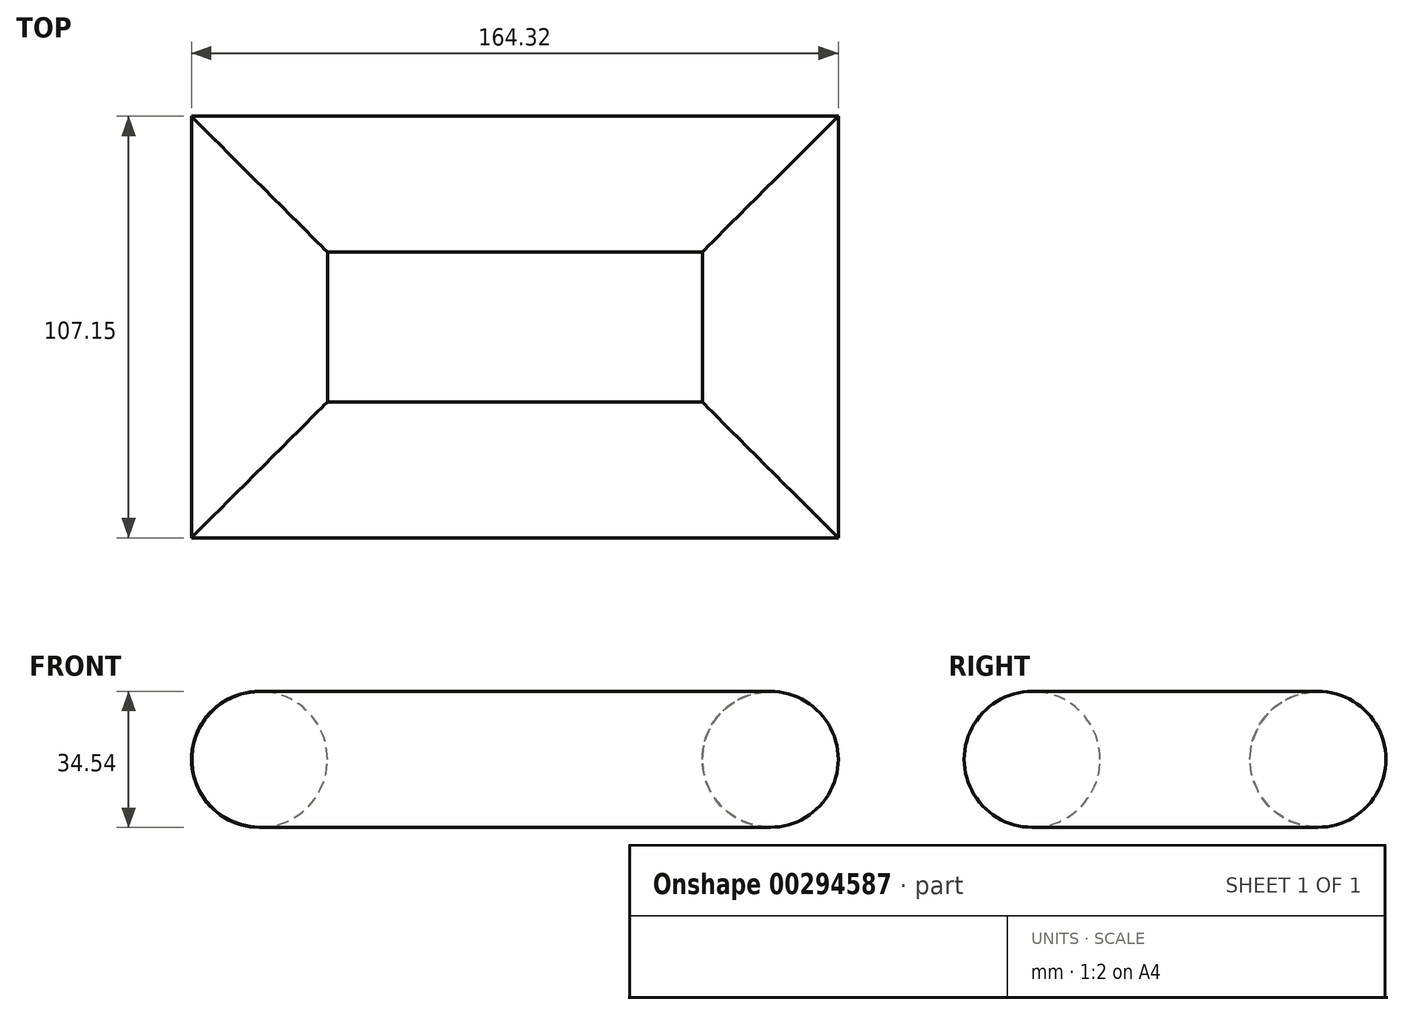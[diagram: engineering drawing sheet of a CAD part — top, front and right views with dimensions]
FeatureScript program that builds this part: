
annotation { "Feature Type Name" : "Feature", "Feature Type Description" : "" }
export const myFeature = defineFeature(function(context is Context, id is Id, definition is map)
    precondition{}
    {
        {
            var Q0;
            Q0=qCreatedBy(makeId("Top.planeOp"),FACE);
            var sketch = newSketch(context, id + "F0", { "sketchPlane" : qUnion([Q0])});
            skLineSegment(sketch, "E0.bottom", {"start": v(-41.45, 23.87) * mm, "end": v(40.59, 23.87) * mm});
            skLineSegment(sketch, "E0.top", {"start": v(-41.45, 48.74) * mm, "end": v(40.59, 48.74) * mm});
            skLineSegment(sketch, "E0.left", {"start": v(-41.45, 23.87) * mm, "end": v(-41.45, 48.74) * mm});
            skLineSegment(sketch, "E0.right", {"start": v(40.59, 23.87) * mm, "end": v(40.59, 48.74) * mm});
            skSolve(sketch);
        }
        {
            var Q0;
            Q0=qCreatedBy(makeId("Right.planeOp"),FACE);
            var sketch = newSketch(context, id + "F1", { "sketchPlane" : qUnion([Q0])});
            skCircle(sketch, "E1", {"center": v(0, 0) * mm, "radius": 17.27 * mm});
            skSolve(sketch);
        }
        {
            var Q0;
            Q0=makeQuery(id+"F1.imprint","IMPRINT",FACE,{"disambiguationData":[TD([[makeQuery(id+"F1.imprint","IMPRINT",EDGE,{"derivedFrom":sQuery(id+"F1.wireOp",EDGE,"E1")}),1.0]])]});
            var Q1;
            Q1=sQuery(id+"F0.wireOp",EDGE,"E0.bottom");
            var Q2;
            Q2=sQuery(id+"F0.wireOp",EDGE,"E0.left");
            var Q3;
            Q3=sQuery(id+"F0.wireOp",EDGE,"E0.top");
            var Q4;
            Q4=sQuery(id+"F0.wireOp",EDGE,"E0.right");
            sweep(context, id + "F2", {"profiles" : qUnion([Q0]), "path" : qUnion([Q1, Q2, Q3, Q4])});
        }
    });
